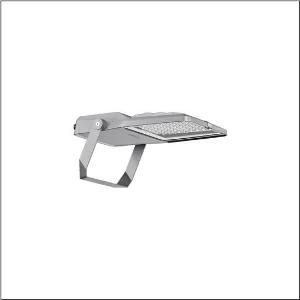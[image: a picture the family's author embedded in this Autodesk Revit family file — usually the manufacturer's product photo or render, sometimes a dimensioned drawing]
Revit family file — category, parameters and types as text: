
# Revit family: floodlight_fl_21_iq_mini___pl61_5xa7771b4c1a_7efd
name_source: partatom
category: Lighting Fixtures
units: mm (PartAtom-declared; Revit-internal decimal feet)

## family parameters
Cut with Voids When Loaded = No
Host = Face
Light Source = No
Part Type = Normal
Room Calculation Point = No
Round Connector Dimension = Use Diameter
Shared = No

## types (1)
- --- (1 x LED, 6370 lm, 45.5 W, 4000K)
    Apparent Load = 46 VA
    CIE Flux Codes = 33 65 98 100 100
    Color Rendering = 70
    Color Temperature = 4000K
    Default Elevation = 1800 mm
    Description = Floodlight FL 21 iQ mini, floodlight, primary light control with lens, of PMMA, primary optical cover: protective disc, of toughened safety glass, transparent, light distribution: PL61, light emission: direct distribution, installation type: surface-mounted, LED, High Power LED, rated luminous flux: 6.370lm, luminous efficacy: 140lm/W, light colour: 740, colour temperature: 4000K, control: Auto-Match, Temp-Guard, Lumen-Switch, Night-Set, Smart-Wire, Light-Fading, Desk-Remote (wireless, voltage-free reading and setting of iQ features in the workshop via application-optimized NFC function/RFID function), optimised constant luminous flux control (CLO 2.0), with terminal, 6-pole, mains connection: 220..240V, AC, 50/60Hz, start of lifetime: 46W, end of service life: 48W, reduction: 22W, luminaire housing, of diecast aluminium, powder-coated, Siteco® metallic grey (DB 702S), corrosivity category C5 mid according to DIN EN ISO 12944, sealing non-destructively replaceable, mounting bracket, of steel, galvanised, powder-coated, Siteco® metallic grey (DB 702S), protection rating (complete): IP66, insulation class (complete): insulation class II (safety insulation), certification: CE, ENEC, VDE, protection symbol: D, impact resistance: IK08, permissible operating ambient temperature: -40..+40°C, permissible operating ambient temperature for outdoor applications: -40..+50°C, standard: DIN EN 12944, LABS conformity tested according to VDMA 24364:2018-05, packaging unit: 1 piece

Light Distribution: PL61
    Height = 70 mm
    Lamp = 1 x LED
    Lamp Light Flux = 6370 lm
    Lamp Power = 45.5 W
    Lamp count = 1
    Length = 485 mm
    Luminous efficacy = 140 lm/W
    Manufacturer = Siteco
    ModVariant = No
    Model = 5XA7771B4C1A
    Mounting Place = Wall
    Mounting Type = Surface mounted
    Number of Poles = 1
    OnlyDefault = Yes
    Power Factor = 1
    Product Name = Floodlight FL 21 iQ mini | PL61
    Product group = floodlight | wall mounted
    ProductGroupID = 2001
    Protection Class = Protection class II
    Protection Degree = IP 66
    RLX_Detail_Level = 1
    RLX_Emergency_Light_Flux = 0 lm
    RLX_Emergency_Type = 0
    RLX_Emergency_Type_DB = No
    RlxData = <blob elided: 96221 chars, md5=09071629>
    Socket = socket
    Standby Power = 0 W
    System Light Flux = 6370 lm
    System Power = 46 W
    Type Comments = factory setting: luminous flux: 100 % | dim-lin: 254 | 463 mA
    Type Image = l_1006845.jpg
    URL = http://relux.com
    VarID = @adj_106875
    Voltage = 0 V
    Weight = 0.00 kg
    Width = 337 mm

## geometry (parser evidence)
native form markers: Blend x4, Sweep x14
no freeform markers — native parametric forms only
